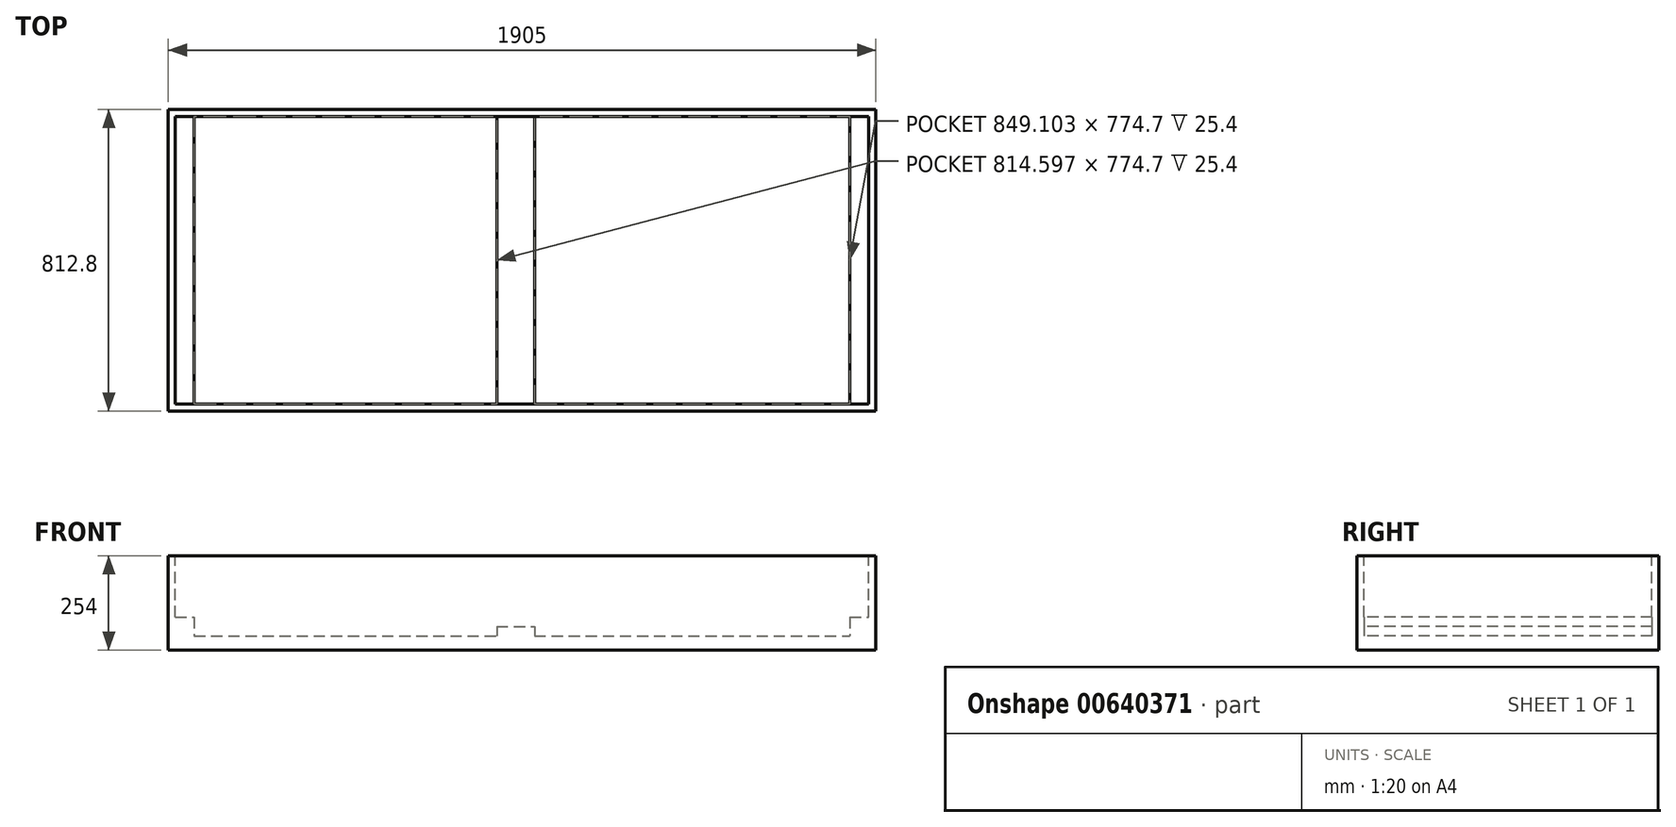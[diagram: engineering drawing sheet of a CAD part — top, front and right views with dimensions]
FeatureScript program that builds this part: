
annotation { "Feature Type Name" : "Feature", "Feature Type Description" : "" }
export const myFeature = defineFeature(function(context is Context, id is Id, definition is map)
    precondition{}
    {
        {
            var Q0;
            Q0=qCreatedBy(makeId("Front.planeOp"),FACE);
            var sketch = newSketch(context, id + "F0", { "sketchPlane" : qUnion([Q0])});
            skLineSegment(sketch, "E0.bottom", {"start": v(-935.25, 128.14) * mm, "end": v(969.75, 128.14) * mm});
            skLineSegment(sketch, "E0.top", {"start": v(-935.25, -125.86) * mm, "end": v(969.75, -125.86) * mm});
            skLineSegment(sketch, "E0.left", {"start": v(-935.25, 128.14) * mm, "end": v(-935.25, -125.86) * mm});
            skLineSegment(sketch, "E0.right", {"start": v(969.75, 128.14) * mm, "end": v(969.75, -125.86) * mm});
            skSolve(sketch);
        }
        {
            var Q0;
            Q0=makeQuery(id+"F0.imprint","IMPRINT",FACE,{"disambiguationData":[TD([[makeQuery(id+"F0.imprint","IMPRINT",EDGE,{"derivedFrom":sQuery(id+"F0.wireOp",EDGE,"E0.bottom")}),-1.0]])]});
            extrude(context, id + "F1", {"entities" : qUnion([Q0]), "endBound" : BoundingType.SYMMETRIC, "depth" : 812.8 * mm, "offsetDistance" : 25.4 * mm});
        }
        {
            var Q0;
            Q0=makeQuery(id+"F1.opExtrude","SWEPT_FACE",FACE,{"disambiguationData":[OSD([sQuery(id+"F0.wireOp",EDGE,"E0.bottom")])]});
            var sketch = newSketch(context, id + "F2", { "sketchPlane" : qUnion([Q0])});
            skLineSegment(sketch, "E1.bottom", {"start": v(-916.2, 387.35) * mm, "end": v(950.7, 387.35) * mm});
            skLineSegment(sketch, "E1.top", {"start": v(-916.2, -387.35) * mm, "end": v(950.7, -387.35) * mm});
            skLineSegment(sketch, "E1.left", {"start": v(-916.2, 387.35) * mm, "end": v(-916.2, -387.35) * mm});
            skLineSegment(sketch, "E1.right", {"start": v(950.7, 387.35) * mm, "end": v(950.7, -387.35) * mm});
            skSolve(sketch);
        }
        {
            var Q0;
            Q0=makeQuery(id+"F2.imprint","IMPRINT",FACE,{"disambiguationData":[TD([[makeQuery(id+"F2.imprint","IMPRINT",EDGE,{"derivedFrom":sQuery(id+"F2.wireOp",EDGE,"E1.bottom")}),-1.0]])]});
            extrude(context, id + "F3", {"entities" : qUnion([Q0]), "operationType" : NewBodyOperationType.REMOVE, "oppositeDirection" : true, "depth" : 215.9 * mm, "offsetDistance" : 25.4 * mm});
        }
        {
            var Q0;
            Q0=makeQuery(id+"F3.boolean.opBoolean","COPY",FACE,{"derivedFrom":makeQuery(id+"F3.opExtrude","CAP_FACE",FACE,{"disambiguationData":[OSD([sQuery(id+"F2.wireOp",EDGE,"E1.bottom"),sQuery(id+"F2.wireOp",EDGE,"E1.top"),sQuery(id+"F2.wireOp",EDGE,"E1.left"),sQuery(id+"F2.wireOp",EDGE,"E1.right")])],"isStart":false})});
            var sketch = newSketch(context, id + "F4", { "sketchPlane" : qUnion([Q0])});
            skLineSegment(sketch, "E2.bottom", {"start": v(950.7, -387.35) * mm, "end": v(899.9, -387.35) * mm});
            skLineSegment(sketch, "E2.top", {"start": v(950.7, 387.35) * mm, "end": v(899.9, 387.35) * mm});
            skLineSegment(sketch, "E2.left", {"start": v(950.7, -387.35) * mm, "end": v(950.7, 387.35) * mm});
            skLineSegment(sketch, "E2.right", {"start": v(899.9, -387.35) * mm, "end": v(899.9, 387.35) * mm});
            skLineSegment(sketch, "E3.bottom", {"start": v(-916.2, -387.35) * mm, "end": v(-865.4, -387.35) * mm});
            skLineSegment(sketch, "E3.top", {"start": v(-916.2, 387.35) * mm, "end": v(-865.4, 387.35) * mm});
            skLineSegment(sketch, "E3.left", {"start": v(-916.2, -387.35) * mm, "end": v(-916.2, 387.35) * mm});
            skLineSegment(sketch, "E3.right", {"start": v(-865.4, -387.35) * mm, "end": v(-865.4, 387.35) * mm});
            skSolve(sketch);
        }
        {
            var Q0;
            Q0=makeQuery(id+"F4.imprint","IMPRINT",FACE,{"disambiguationData":[TD([[makeQuery(id+"F4.imprint","IMPRINT",EDGE,{"derivedFrom":sQuery(id+"F4.wireOp",EDGE,"E3.bottom")}),1.0]])]});
            var Q1;
            Q1=makeQuery(id+"F4.imprint","IMPRINT",FACE,{"disambiguationData":[TD([[makeQuery(id+"F4.imprint","IMPRINT",EDGE,{"derivedFrom":sQuery(id+"F4.wireOp",EDGE,"E2.bottom")}),1.0]])]});
            extrude(context, id + "F5", {"entities" : qUnion([Q0, Q1]), "operationType" : NewBodyOperationType.ADD, "depth" : 50.8 * mm, "offsetDistance" : 25.4 * mm});
        }
        {
            var Q0;
            Q0=makeQuery(id+"F3.boolean.opBoolean","COPY",FACE,{"derivedFrom":makeQuery(id+"F3.opExtrude","CAP_FACE",FACE,{"disambiguationData":[OSD([sQuery(id+"F2.wireOp",EDGE,"E1.bottom"),sQuery(id+"F2.wireOp",EDGE,"E1.top"),sQuery(id+"F2.wireOp",EDGE,"E1.left"),sQuery(id+"F2.wireOp",EDGE,"E1.right")])],"isStart":false})});
            var sketch = newSketch(context, id + "F6", { "sketchPlane" : qUnion([Q0])});
            skLineSegment(sketch, "E4.bottom", {"start": v(-50.8, 387.35) * mm, "end": v(50.8, 387.35) * mm});
            skLineSegment(sketch, "E4.top", {"start": v(-50.8, -387.35) * mm, "end": v(50.8, -387.35) * mm});
            skLineSegment(sketch, "E4.left", {"start": v(-50.8, 387.35) * mm, "end": v(-50.8, -387.35) * mm});
            skLineSegment(sketch, "E4.right", {"start": v(50.8, 387.35) * mm, "end": v(50.8, -387.35) * mm});
            skSolve(sketch);
        }
        {
            var Q0;
            Q0=makeQuery(id+"F6.imprint","IMPRINT",FACE,{"disambiguationData":[TD([[makeQuery(id+"F6.imprint","IMPRINT",EDGE,{"derivedFrom":sQuery(id+"F6.wireOp",EDGE,"E4.bottom")}),-1.0]])]});
            extrude(context, id + "F7", {"entities" : qUnion([Q0]), "operationType" : NewBodyOperationType.ADD, "depth" : 25.4 * mm, "offsetDistance" : 25.4 * mm});
        }
    });
